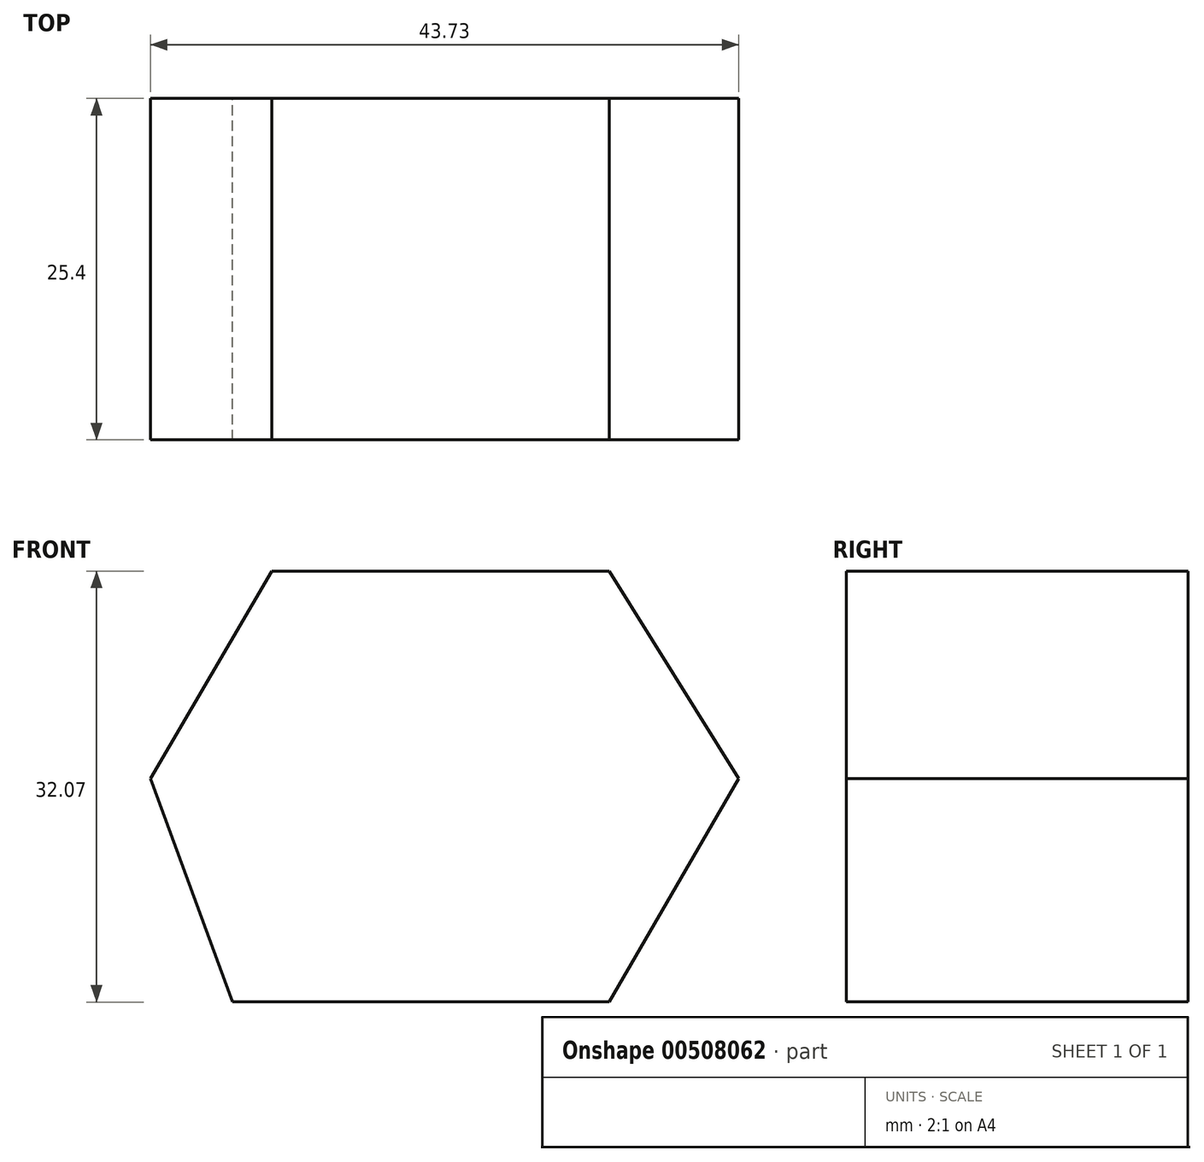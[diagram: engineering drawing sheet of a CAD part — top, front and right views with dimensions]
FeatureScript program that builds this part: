
annotation { "Feature Type Name" : "Feature", "Feature Type Description" : "" }
export const myFeature = defineFeature(function(context is Context, id is Id, definition is map)
    precondition{}
    {
        {
            var Q0;
            Q0=qCreatedBy(makeId("Front.planeOp"),FACE);
            var sketch = newSketch(context, id + "F0", { "sketchPlane" : qUnion([Q0])});
            skLineSegment(sketch, "E0", {"start": v(-11.95, 37.75) * mm, "end": v(13.12, 37.75) * mm});
            skLineSegment(sketch, "E1", {"start": v(13.12, 37.75) * mm, "end": v(22.74, 22.3) * mm});
            skLineSegment(sketch, "E2", {"start": v(22.74, 22.3) * mm, "end": v(13.12, 5.68) * mm});
            skLineSegment(sketch, "E3", {"start": v(-11.95, 37.75) * mm, "end": v(-20.99, 22.3) * mm});
            skLineSegment(sketch, "E4", {"start": v(-20.99, 22.3) * mm, "end": v(-14.87, 5.68) * mm});
            skLineSegment(sketch, "E5", {"start": v(-14.87, 5.68) * mm, "end": v(13.12, 5.68) * mm});
            skSolve(sketch);
        }
        {
            var Q0;
            Q0 = qSketchRegion(id + "F0", true);
            extrude(context, id + "F1", {"entities" : qUnion([Q0]), "endBound" : BoundingType.SYMMETRIC, "depth" : 25.4 * mm});
        }
    });
